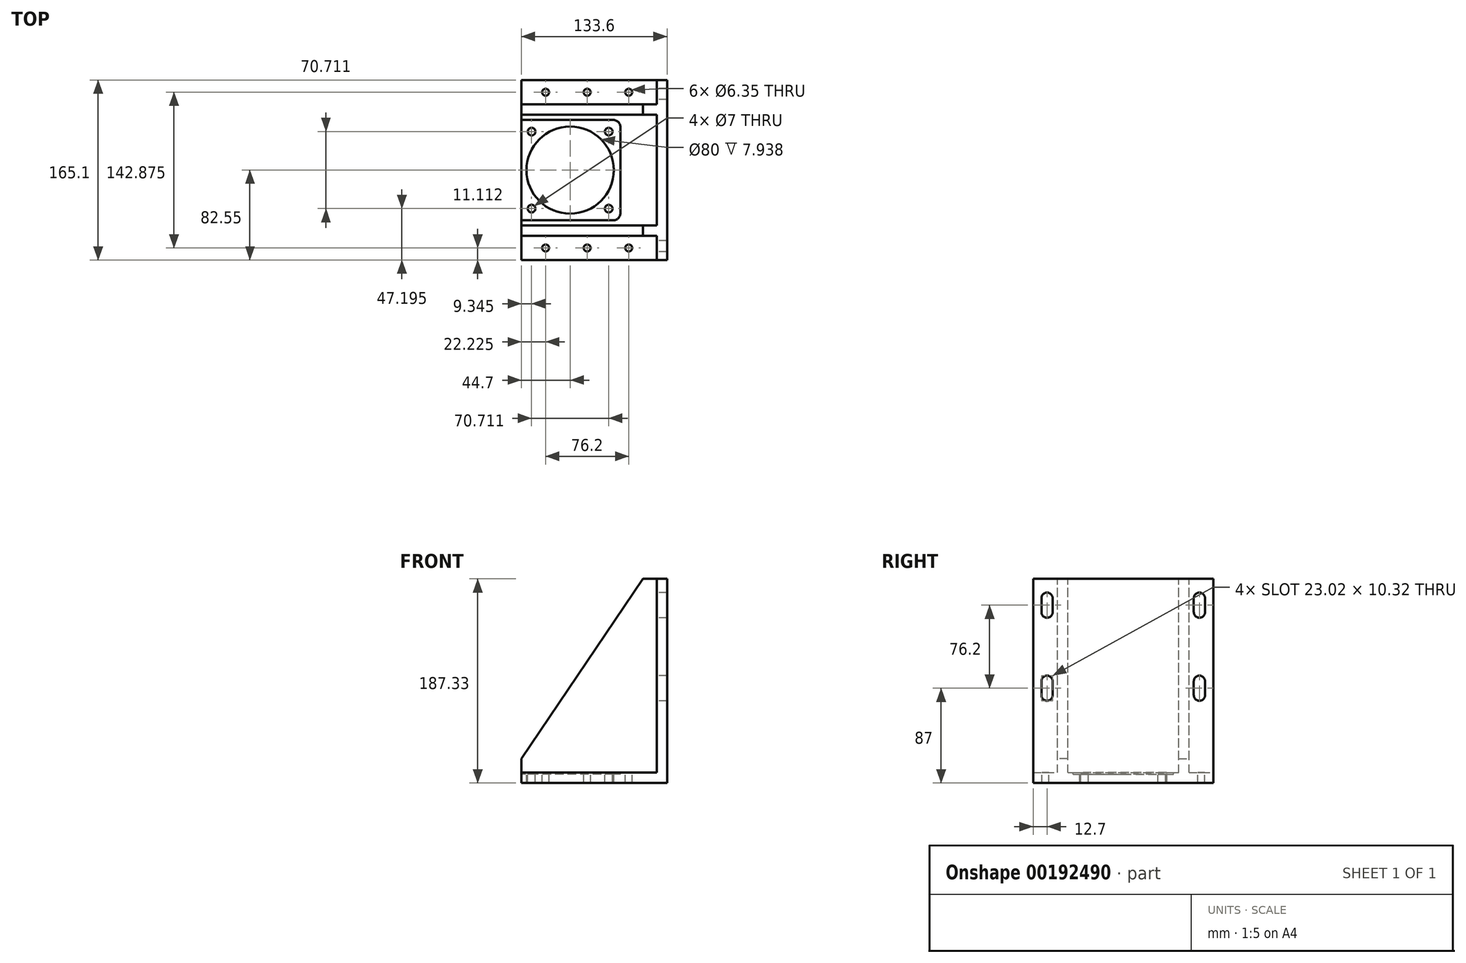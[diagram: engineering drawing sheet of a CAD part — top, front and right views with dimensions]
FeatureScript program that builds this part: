
annotation { "Feature Type Name" : "Feature", "Feature Type Description" : "" }
export const myFeature = defineFeature(function(context is Context, id is Id, definition is map)
    precondition{}
    {
        {
            var Q0;
            Q0=qCreatedBy(makeId("Top.planeOp"),FACE);
            var sketch = newSketch(context, id + "F0", { "sketchPlane" : qUnion([Q0])});
            skPoint(sketch, "E0.middle", {"position": v(0, 0) * mm});
            skCircle(sketch, "E1", {"center": v(-35.36, 35.36) * mm, "radius": 3.5 * mm});
            skCircle(sketch, "E2.1.0", {"center": v(-35.36, -35.36) * mm, "radius": 3.5 * mm});
            skCircle(sketch, "E2.2.0", {"center": v(35.36, -35.36) * mm, "radius": 3.5 * mm});
            skCircle(sketch, "E2.3.0", {"center": v(35.36, 35.36) * mm, "radius": 3.5 * mm});
            skLineSegment(sketch, "E3", {"start": v(88.9, 82.55) * mm, "end": v(-44.7, 82.55) * mm});
            skLineSegment(sketch, "E4", {"start": v(88.9, 82.55) * mm, "end": v(88.9, -82.55) * mm});
            skLineSegment(sketch, "E5", {"start": v(-44.7, 82.55) * mm, "end": v(-44.7, -82.55) * mm});
            skLineSegment(sketch, "E6", {"start": v(-44.7, -82.55) * mm, "end": v(88.9, -82.55) * mm});
            skCircle(sketch, "E7", {"center": v(0, 0) * mm, "radius": 50 * mm, "construction": true});
            skSolve(sketch);
        }
        {
            var Q0;
            Q0 = qSketchRegion(id + "F0", true);
            extrude(context, id + "F1", {"entities" : qUnion([Q0]), "oppositeDirection" : true, "depth" : 9.52 * mm});
        }
        {
            var Q0;
            Q0=qCreatedBy(makeId("Top.planeOp"),FACE);
            var sketch = newSketch(context, id + "F2", { "sketchPlane" : qUnion([Q0])});
            skCircle(sketch, "E8", {"center": v(0, 0) * mm, "radius": 40 * mm});
            skSolve(sketch);
        }
        {
            var Q0;
            Q0 = qSketchRegion(id + "F2", true);
            extrude(context, id + "F3", {"entities" : qUnion([Q0]), "operationType" : NewBodyOperationType.REMOVE, "endBound" : BoundingType.THROUGH_ALL, "oppositeDirection" : true, "depth" : 2.74 * mm});
        }
        {
            var Q0;
            Q0=makeQuery(id+"F1.opExtrude","SWEPT_FACE",FACE,{"disambiguationData":[OSD([sQuery(id+"F0.wireOp",EDGE,"E6")])]});
            cPlane(context, id + "F4", {"entities" : qUnion([Q0]), "cplaneType" : CPlaneType.OFFSET, "offset" : 22.22 * mm, "oppositeDirection" : true, "width" : 152.4 * mm, "height" : 152.4 * mm});
        }
        {
            var Q0;
            Q0=qCreatedBy(id+"F4.planeOp",FACE);
            var sketch = newSketch(context, id + "F5", { "sketchPlane" : qUnion([Q0])});
            skLineSegment(sketch, "E9", {"start": v(-44.7, 0) * mm, "end": v(79.38, 0) * mm});
            skLineSegment(sketch, "E10", {"start": v(79.38, 0) * mm, "end": v(79.38, 177.8) * mm});
            skLineSegment(sketch, "E11", {"start": v(66.68, 177.8) * mm, "end": v(79.38, 177.8) * mm});
            skLineSegment(sketch, "E12", {"start": v(-44.7, 0) * mm, "end": v(-44.7, 12.7) * mm});
            skLineSegment(sketch, "E13", {"start": v(-44.7, 12.7) * mm, "end": v(66.68, 177.8) * mm});
            skSolve(sketch);
        }
        {
            var Q0;
            Q0 = qSketchRegion(id + "F5", true);
            extrude(context, id + "F6", {"entities" : qUnion([Q0]), "operationType" : NewBodyOperationType.ADD, "oppositeDirection" : true, "depth" : 9.52 * mm});
        }
        {
            var Q0;
            Q0=makeQuery(id+"F1.opExtrude","SWEPT_FACE",FACE,{"disambiguationData":[OSD([sQuery(id+"F0.wireOp",EDGE,"E3")])]});
            cPlane(context, id + "F7", {"entities" : qUnion([Q0]), "cplaneType" : CPlaneType.OFFSET, "offset" : 22.22 * mm, "oppositeDirection" : true, "width" : 152.4 * mm, "height" : 152.4 * mm});
        }
        {
            var Q0;
            Q0=qCreatedBy(id+"F7.planeOp",FACE);
            var sketch = newSketch(context, id + "F8", { "sketchPlane" : qUnion([Q0])});
            skLineSegment(sketch, "E14.0", {"start": v(44.7, 12.7) * mm, "end": v(-66.68, 177.8) * mm});
            skLineSegment(sketch, "E15.0", {"start": v(-79.38, 0) * mm, "end": v(-79.38, 177.8) * mm});
            skPoint(sketch, "E16.0", {"position": v(-66.68, 177.8) * mm});
            skLineSegment(sketch, "E17.0", {"start": v(-66.68, 177.8) * mm, "end": v(-79.38, 177.8) * mm});
            skLineSegment(sketch, "E18.0", {"start": v(44.7, 0) * mm, "end": v(44.7, 12.7) * mm});
            skLineSegment(sketch, "E19.0", {"start": v(44.7, 0) * mm, "end": v(-79.37, 0) * mm});
            skSolve(sketch);
        }
        {
            var Q0;
            Q0 = qSketchRegion(id + "F8", true);
            extrude(context, id + "F9", {"entities" : qUnion([Q0]), "operationType" : NewBodyOperationType.ADD, "oppositeDirection" : true, "depth" : 9.52 * mm});
        }
        {
            var Q0;
            Q0=makeQuery(id+"F9.opExtrude","SWEPT_FACE",FACE,{"disambiguationData":[OSD([sQuery(id+"F8.wireOp",EDGE,"E15.0")])]});
            var sketch = newSketch(context, id + "F10", { "sketchPlane" : qUnion([Q0])});
            skLineSegment(sketch, "E20.0", {"start": v(82.55, 0) * mm, "end": v(-82.55, 0) * mm});
            skLineSegment(sketch, "E21", {"start": v(-82.55, 0) * mm, "end": v(-82.55, 177.8) * mm});
            skLineSegment(sketch, "E22", {"start": v(82.55, 177.8) * mm, "end": v(82.55, 0) * mm});
            skLineSegment(sketch, "E23", {"start": v(-82.55, 177.8) * mm, "end": v(82.55, 177.8) * mm});
            skArc(sketch, "E24", {"start": v(75, 160.02) * mm, "mid": v(69.85, 165.18) * mm, "end": v(64.7, 160.02) * mm});
            skArc(sketch, "E25", {"start": v(64.7, 147.32) * mm, "mid": v(69.85, 142.16) * mm, "end": v(75, 147.32) * mm});
            skLineSegment(sketch, "E26", {"start": v(64.7, 147.32) * mm, "end": v(64.7, 160.02) * mm});
            skLineSegment(sketch, "E27", {"start": v(75, 147.32) * mm, "end": v(75, 160.02) * mm});
            skArc(sketch, "E28.0.1.0", {"start": v(64.7, 71.12) * mm, "mid": v(69.85, 65.96) * mm, "end": v(75, 71.12) * mm});
            skLineSegment(sketch, "E28.0.1.1", {"start": v(64.7, 71.12) * mm, "end": v(64.7, 83.82) * mm});
            skArc(sketch, "E28.0.1.2", {"start": v(75, 83.82) * mm, "mid": v(69.85, 88.98) * mm, "end": v(64.7, 83.82) * mm});
            skLineSegment(sketch, "E28.0.1.3", {"start": v(75, 71.12) * mm, "end": v(75, 83.82) * mm});
            skArc(sketch, "E28.1.0.0", {"start": v(-75, 147.32) * mm, "mid": v(-69.85, 142.16) * mm, "end": v(-64.7, 147.32) * mm});
            skLineSegment(sketch, "E28.1.0.1", {"start": v(-75, 147.32) * mm, "end": v(-75, 160.02) * mm});
            skArc(sketch, "E28.1.0.2", {"start": v(-64.7, 160.02) * mm, "mid": v(-69.85, 165.18) * mm, "end": v(-75, 160.02) * mm});
            skLineSegment(sketch, "E28.1.0.3", {"start": v(-64.7, 147.32) * mm, "end": v(-64.7, 160.02) * mm});
            skArc(sketch, "E28.1.1.0", {"start": v(-75, 71.12) * mm, "mid": v(-69.85, 65.96) * mm, "end": v(-64.7, 71.12) * mm});
            skLineSegment(sketch, "E28.1.1.1", {"start": v(-75, 71.12) * mm, "end": v(-75, 83.82) * mm});
            skArc(sketch, "E28.1.1.2", {"start": v(-64.7, 83.82) * mm, "mid": v(-69.85, 88.98) * mm, "end": v(-75, 83.82) * mm});
            skLineSegment(sketch, "E28.1.1.3", {"start": v(-64.7, 71.12) * mm, "end": v(-64.7, 83.82) * mm});
            skLineSegment(sketch, "E28.direction1", {"start": v(64.7, 147.32) * mm, "end": v(-75, 147.32) * mm, "construction": true});
            skLineSegment(sketch, "E28.direction2", {"start": v(64.7, 147.32) * mm, "end": v(64.7, 71.12) * mm, "construction": true});
            skSolve(sketch);
        }
        {
            var Q0;
            Q0 = qSketchRegion(id + "F10", true);
            extrude(context, id + "F11", {"entities" : qUnion([Q0]), "operationType" : NewBodyOperationType.ADD, "depth" : 9.52 * mm});
        }
        {
            var Q0;
            {var subQ2=sQuery(id+"F0.wireOp",EDGE,"E5");var subQ3=sQuery(id+"F0.wireOp",EDGE,"E1");var subQ4=sQuery(id+"F0.wireOp",EDGE,"E2.1.0");var subQ5=sQuery(id+"F0.wireOp",EDGE,"E2.2.0");var subQ6=sQuery(id+"F0.wireOp",EDGE,"E2.3.0");Q0=makeQuery(id+"F11.boolean.opBoolean","SPLIT",FACE,{"disambiguationData":[TD([makeQuery(id+"F1.opExtrude","SWEPT_FACE",FACE,{"disambiguationData":[OSD([subQ3])]})])],"derivedFrom":makeQuery(id+"F1.opExtrude","CAP_FACE",FACE,{"disambiguationData":[OSD([subQ3,subQ4,subQ5,subQ6,sQuery(id+"F0.wireOp",EDGE,"E3"),sQuery(id+"F0.wireOp",EDGE,"E4"),subQ2,sQuery(id+"F0.wireOp",EDGE,"E6")])],"isStart":true})});}
            var sketch = newSketch(context, id + "F12", { "sketchPlane" : qUnion([Q0])});
            skLineSegment(sketch, "E29.bottom", {"start": v(39.65, 46) * mm, "end": v(-44.7, 46) * mm});
            skLineSegment(sketch, "E29.top", {"start": v(39.65, -46) * mm, "end": v(-44.7, -46) * mm});
            skLineSegment(sketch, "E29.left", {"start": v(46, 39.65) * mm, "end": v(46, -39.65) * mm});
            skPoint(sketch, "E29.middle", {"position": v(0, 0) * mm});
            skLineSegment(sketch, "E30", {"start": v(-44.7, 46) * mm, "end": v(-44.7, -46) * mm});
            skPoint(sketch, "E31.visualSharp", {"position": v(46, 46) * mm});
            skArc(sketch, "E31.filletArc", {"start": v(46, 39.65) * mm, "mid": v(44.14, 44.14) * mm, "end": v(39.65, 46) * mm});
            skPoint(sketch, "E32.visualSharp", {"position": v(46, -46) * mm});
            skArc(sketch, "E32.filletArc", {"start": v(39.65, -46) * mm, "mid": v(44.14, -44.14) * mm, "end": v(46, -39.65) * mm});
            skSolve(sketch);
        }
        {
            var Q0;
            Q0 = qSketchRegion(id + "F12", true);
            extrude(context, id + "F13", {"entities" : qUnion([Q0]), "operationType" : NewBodyOperationType.REMOVE, "oppositeDirection" : true, "depth" : 1.59 * mm});
        }
        {
            var Q0;
            {var subQ2=sQuery(id+"F0.wireOp",EDGE,"E6");var subQ3=sQuery(id+"F0.wireOp",EDGE,"E5");Q0=makeQuery(id+"F11.boolean.opBoolean","SPLIT",FACE,{"disambiguationData":[TD([makeQuery(id+"F1.opExtrude","SWEPT_FACE",FACE,{"disambiguationData":[OSD([subQ2])]})])],"derivedFrom":makeQuery(id+"F1.opExtrude","CAP_FACE",FACE,{"disambiguationData":[OSD([sQuery(id+"F0.wireOp",EDGE,"E1"),sQuery(id+"F0.wireOp",EDGE,"E2.1.0"),sQuery(id+"F0.wireOp",EDGE,"E2.2.0"),sQuery(id+"F0.wireOp",EDGE,"E2.3.0"),sQuery(id+"F0.wireOp",EDGE,"E3"),sQuery(id+"F0.wireOp",EDGE,"E4"),subQ3,subQ2])],"isStart":true})});}
            var sketch = newSketch(context, id + "F14", { "sketchPlane" : qUnion([Q0])});
            skCircle(sketch, "E33", {"center": v(-22.48, -71.44) * mm, "radius": 3.18 * mm});
            skCircle(sketch, "E34.0.1.0", {"center": v(-22.48, 71.44) * mm, "radius": 3.18 * mm});
            skCircle(sketch, "E34.1.0.0", {"center": v(15.62, -71.44) * mm, "radius": 3.18 * mm});
            skCircle(sketch, "E34.1.1.0", {"center": v(15.62, 71.44) * mm, "radius": 3.18 * mm});
            skCircle(sketch, "E34.2.0.0", {"center": v(53.72, -71.44) * mm, "radius": 3.18 * mm});
            skCircle(sketch, "E34.2.1.0", {"center": v(53.72, 71.44) * mm, "radius": 3.18 * mm});
            skLineSegment(sketch, "E34.direction1", {"start": v(-22.48, -71.44) * mm, "end": v(15.62, -71.44) * mm, "construction": true});
            skLineSegment(sketch, "E34.direction2", {"start": v(-22.48, -71.44) * mm, "end": v(-22.48, 71.44) * mm, "construction": true});
            skSolve(sketch);
        }
        {
            var Q0;
            Q0 = qSketchRegion(id + "F14", true);
            extrude(context, id + "F15", {"entities" : qUnion([Q0]), "operationType" : NewBodyOperationType.REMOVE, "endBound" : BoundingType.THROUGH_ALL, "oppositeDirection" : true, "depth" : 25.4 * mm});
        }
    });
